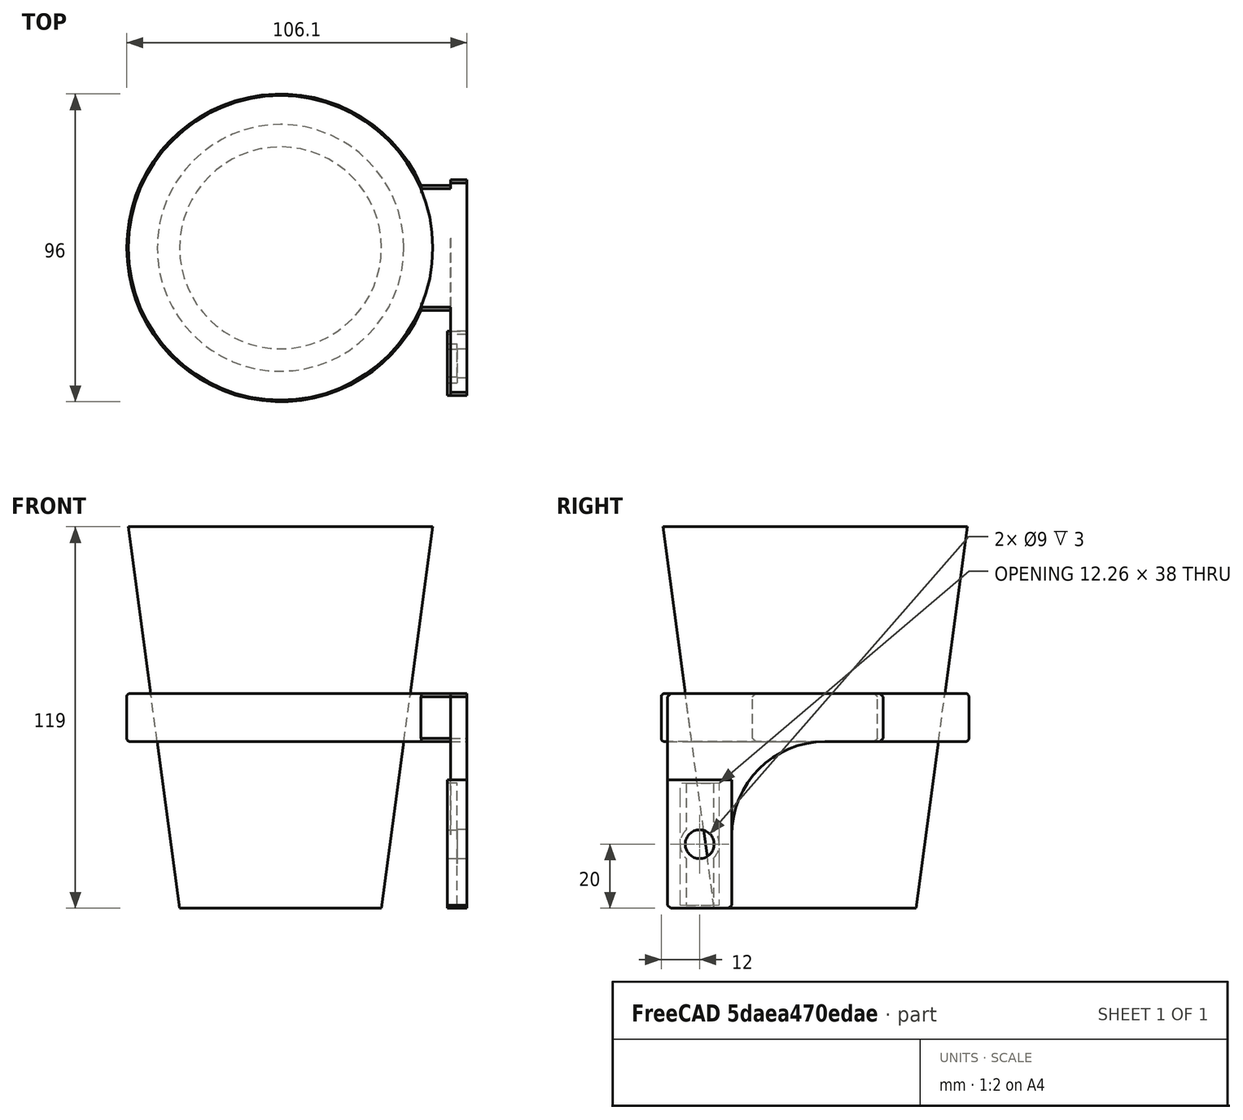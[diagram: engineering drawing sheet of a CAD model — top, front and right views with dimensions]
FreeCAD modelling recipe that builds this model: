
FCSTD DOCUMENT  (FreeCAD 0.21R33668 +26 (Git))
Label: Cup Holder
License: All rights reserved
LicenseURL: https://en.wikipedia.org/wiki/All_rights_reserved
objects: Part::Cut×9, Part::Box×8, Part::Cylinder×4, Part::Chamfer×4, Part::Cone×2, Part::Fillet×2, Part::MultiFuse×2, Part::FeaturePython×1
note: 32 computed .brp shape members not serialized (recipe doc carries the construction recipe); baked Part::Feature solids carry a one-line shape summary decoded from their .brp

FEATURE [Part::Cone] Cone  label="Cup Mold"
  Angle = 360
  AttacherType = Attacher::AttachEngine3D
  Height = 119
  Radius1 = 31.5
  Radius2 = 47.5
FEATURE [Part::FeaturePython] Tube  # WARN: FeaturePython — macro-defined, semantics opaque (R4)
  AttacherType = Attacher::AttachEngine3D
  Height = 15
  InnerRadius = 38
  OuterRadius = 48
  Placement = pos=(0,0,52) rot=(0,0,1;0rad)
FEATURE [Part::Box] Box  label="Cube"
  AttacherType = Attacher::AttachEngine3D
  Height = 67
  Length = 5
  Placement = pos=(50.1,-46,0) rot=(0,0,1;0rad)
  Width = 67.29
FEATURE [Part::Box] Box003  label="Cube003"
  AttacherType = Attacher::AttachEngine3D
  Height = 52
  Length = 10.4
  Placement = pos=(45.7,-26,0) rot=(0,0,1;0rad)
  Width = 58.22
FEATURE [Part::Fillet] Fillet001
  Base = -> Box003
  Edges = 1 edges r=29.11: [Edge10]
FEATURE [Part::Cylinder] Cylinder
  Angle = 360
  AttacherType = Attacher::AttachEngine3D
  FirstAngle = 0
  Height = 10
  Radius = 4.5
  SecondAngle = 0
FEATURE [Part::Box] Box004  label="Cube004"
  AttacherType = Attacher::AttachEngine3D
  Height = 6
  Length = 40
  Placement = pos=(-20,-10,0) rot=(0,0,1;0rad)
  Width = 20
FEATURE [Part::Cut] Cut003
  Base = -> Box004
  Tool = -> Cylinder
FEATURE [Part::Cylinder] Cylinder001
  Angle = 360
  AttacherType = Attacher::AttachEngine3D
  FirstAngle = 0
  Height = 10
  Placement = pos=(0,0,3) rot=(0,0,1;0rad)
  Radius = 6.13
  SecondAngle = 0
FEATURE [Part::Cut] Cut004
  Base = -> Cut003
  Tool = -> Cylinder001
FEATURE [Part::Box] Box005  label="Cube005"
  AttacherType = Attacher::AttachEngine3D
  Height = 10
  Length = 38
  Placement = pos=(-19,-4.25,3) rot=(0,0,1;0rad)
  Width = 8.5
FEATURE [Part::Cut] Cut005  label="Servo Mount Unfinished"
  Base = -> Cut004
  Placement = pos=(55.1,-36,20) rot=(0,-1,0;1.5708rad)
  Tool = -> Box005
FEATURE [Part::Box] Box006  label="Cube006"
  AttacherType = Attacher::AttachEngine3D
  Height = 15
  Length = 9.3
  Placement = pos=(40.8,-19.5,52) rot=(0,0,1;0rad)
  Width = 39
FEATURE [Part::Cut] Cut
  Base = -> Tube
  Tool = -> Cone
FEATURE [Part::Fillet] Fillet  label="Rounded Holder"
  Base = -> Cut
  Edges = 3 edges r=1: [Edge1,Edge3,Edge4]
  Placement = pos=(-3,0,0) rot=(0,0,1;0rad)
FEATURE [Part::Chamfer] Chamfer003  label="Holder Holder"
  Base = -> Box006
  Edges = 4 edges r=1: [Edge9,Edge10,Edge11,Edge12]
FEATURE [Part::Cone] Cone001  label="Cup"
  Angle = 360
  AttacherType = Attacher::AttachEngine3D
  Height = 119
  Placement = pos=(-3,0,0) rot=(0,0,1;0rad)
  Radius1 = 31.5
  Radius2 = 47.5
FEATURE [Part::Box] Box007  label="Cube007"
  AttacherType = Attacher::AttachEngine3D
  Height = 6
  Length = 40
  Placement = pos=(-20,-10,0) rot=(0,0,1;0rad)
  Width = 20
FEATURE [Part::Box] Box008  label="Cube008"
  AttacherType = Attacher::AttachEngine3D
  Height = 10
  Length = 38
  Placement = pos=(-19,-4.25,3) rot=(0,0,1;0rad)
  Width = 8.5
FEATURE [Part::Cylinder] Cylinder002
  Angle = 360
  AttacherType = Attacher::AttachEngine3D
  FirstAngle = 0
  Height = 10
  Radius = 4.5
  SecondAngle = 0
FEATURE [Part::Cut] Cut007
  Base = -> Box007
  Tool = -> Cylinder002
FEATURE [Part::Cylinder] Cylinder003
  Angle = 360
  AttacherType = Attacher::AttachEngine3D
  FirstAngle = 0
  Height = 10
  Placement = pos=(0,0,3) rot=(0,0,1;0rad)
  Radius = 6.13
  SecondAngle = 0
FEATURE [Part::Cut] Cut008
  Base = -> Cut007
  Tool = -> Cylinder003
FEATURE [Part::Cut] Cut009  label="Servo Mount Unfinished001"
  Base = -> Cut008
  Placement = pos=(55.1,-36,20) rot=(0,-1,0;1.5708rad)
  Tool = -> Box008
FEATURE [Part::Box] Box002  label="Cube002"
  AttacherType = Attacher::AttachEngine3D
  Height = 40
  Length = 6
  Placement = pos=(50.1,-46,0) rot=(0,0,1;0rad)
  Width = 20
FEATURE [Part::Cut] Cut001
  Base = -> Box
  Tool = -> Box002
FEATURE [Part::Cut] Cut006  label="Servo Arch"
  Base = -> Cut001
  Tool = -> Fillet001
FEATURE [Part::Chamfer] Chamfer004
  Base = -> Cut006
  Edges = 3 edges r=1: [Edge10,Edge11,Edge14]
FEATURE [Part::MultiFuse] Fusion  label="Complete Holded Holder"
  Shapes = -> [Chamfer003,Fillet,Chamfer004]
FEATURE [Part::Chamfer] Chamfer  label="Servo Mount"
  Base = -> Cut005
  Edges = 2 edges r=1: [Edge1,Edge3]
FEATURE [Part::Chamfer] Chamfer005  label="Servo Mount Standalone"
  Base = -> Cut009
  Edges = 2 edges r=1: [Edge1,Edge3]
FEATURE [Part::MultiFuse] Fusion001  label="Complete Cup Holder"
  Shapes = -> [Fusion,Chamfer]
